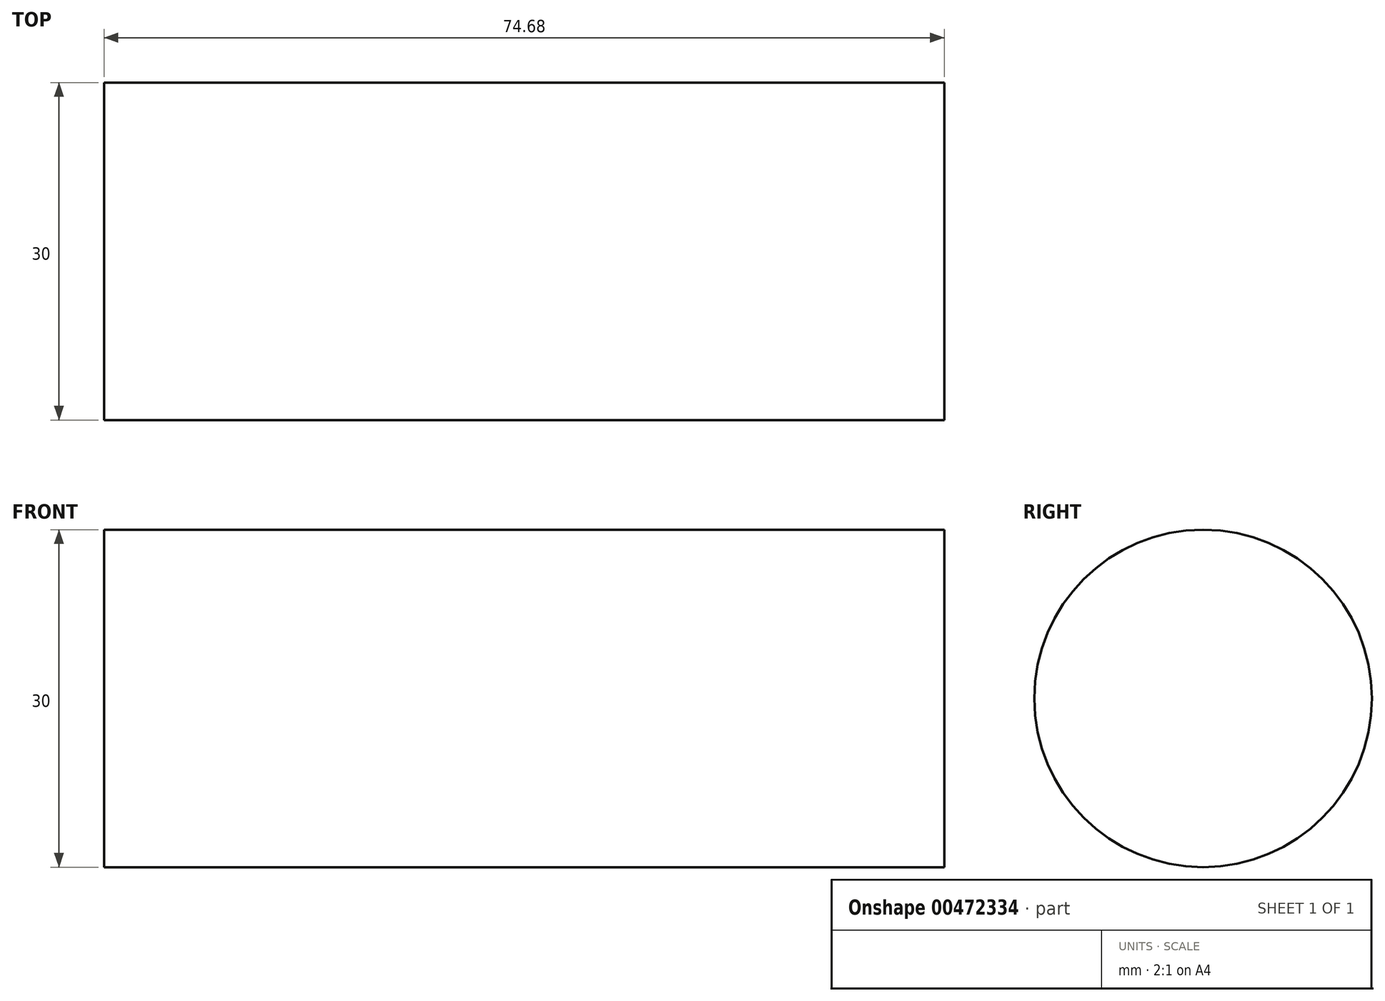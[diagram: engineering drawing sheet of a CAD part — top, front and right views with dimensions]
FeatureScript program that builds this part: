
annotation { "Feature Type Name" : "Feature", "Feature Type Description" : "" }
export const myFeature = defineFeature(function(context is Context, id is Id, definition is map)
    precondition{}
    {
        {
            var Q0;
            Q0=qCreatedBy(makeId("Right.planeOp"),FACE);
            var sketch = newSketch(context, id + "F0", { "sketchPlane" : qUnion([Q0])});
            skCircle(sketch, "E0", {"center": v(0, 0) * mm, "radius": 15 * mm});
            skSolve(sketch);
        }
        {
            var Q0;
            Q0 = qSketchRegion(id + "F0", true);
            extrude(context, id + "F1", {"entities" : qUnion([Q0]), "oppositeDirection" : true, "depth" : 74.68 * mm});
        }
    });
